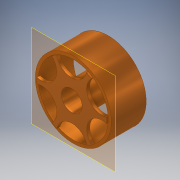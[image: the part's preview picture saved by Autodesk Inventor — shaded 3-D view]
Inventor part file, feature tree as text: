
AUTODESK INVENTOR PART (.ipt)
format: ipt  version: 2017 (Build 210142000, 142)  size: 174,080 bytes
history: native  units: in
note: dims shown in document units (in); Inventor stores cm internally (conversion verified against a paired STEP export)
features: extrude x3, sketch x3, projected_geometry x2, plane x1, pattern_circular x1
ambient origin geometry x8: Origin, YZ Plane, XZ Plane, XY Plane, X Axis, Y Axis, Z Axis, Center Point
bodies: Solid1 (feature_tree)
feature tree (10):
  extrude  "Extrusion1"  Depth=0.05in
  plane  "Work Plane1"
  extrude  "Extrusion2"  Depth=0.05in
  extrude  "Extrusion3"  TaperAngle=0.0deg  [1 undecoded]
  pattern_circular  "Circular Pattern1"  [2 undecoded]
  sketch  "Sketch1"  dims[d0=0.44in d1=0.05in]
  sketch  "Sketch2"  dims[d2=0.35in d3=0.05in]
  projected_geometry  "Projected Loop1"
  projected_geometry  "Projected Loop2"
  sketch  "Sketch3"  dims[d4=0.57in d5=0.0in d6=0.0in d7=0.05in d8=0.0in d9=0.5in d10=0.05in d11=0.0in d12=2.3622in d13=360.0deg]
note: 3 required parameter values undecoded (feature->parameter linkage not recoverable at this tier; creation-order binding heuristic only, values carry confidence <= 0.55)
